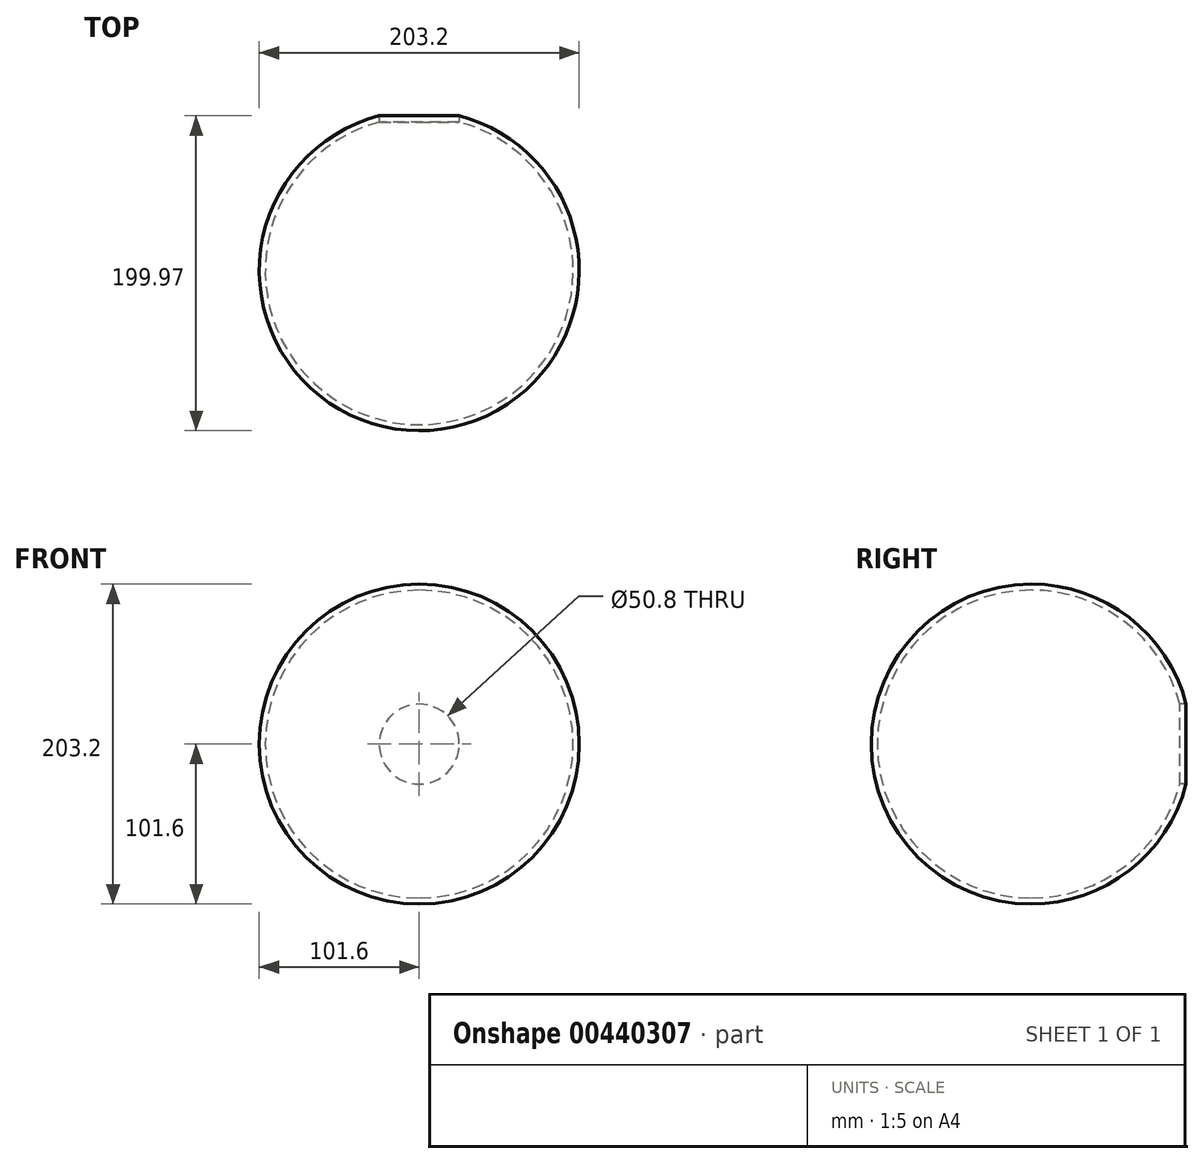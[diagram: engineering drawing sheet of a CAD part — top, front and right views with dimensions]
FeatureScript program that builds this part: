
annotation { "Feature Type Name" : "Feature", "Feature Type Description" : "" }
export const myFeature = defineFeature(function(context is Context, id is Id, definition is map)
    precondition{}
    {
        {
            var Q0;
            Q0=qCreatedBy(makeId("Front.planeOp"),FACE);
            var sketch = newSketch(context, id + "F0", { "sketchPlane" : qUnion([Q0])});
            skArc(sketch, "E0", {"start": v(0, -101.6) * mm, "mid": v(101.6, 0) * mm, "end": v(0, 101.6) * mm});
            skLineSegment(sketch, "E1", {"start": v(0, -97.8) * mm, "end": v(0, -101.6) * mm});
            skLineSegment(sketch, "E2", {"start": v(0, -101.6) * mm, "end": v(0, -97.8) * mm});
            skArc(sketch, "E3", {"start": v(0, -97.8) * mm, "mid": v(97.8, 0) * mm, "end": v(0, 97.8) * mm});
            skLineSegment(sketch, "E4.trimOffspring", {"start": v(0, 97.8) * mm, "end": v(0, 101.6) * mm});
            skSolve(sketch);
        }
        {
            var Q0;
            Q0=qCreatedBy(makeId("Front.planeOp"),FACE);
            var sketch = newSketch(context, id + "F1", { "sketchPlane" : qUnion([Q0])});
            skCircle(sketch, "E5", {"center": v(0, 0) * mm, "radius": 25.4 * mm});
            skLineSegment(sketch, "E6", {"start": v(0, 0) * mm, "end": v(0, 25.4) * mm});
            skSolve(sketch);
        }
        {
            var Q0;
            Q0 = qBodyType(qCreatedBy(id + "F1" ,EDGE), BodyType.WIRE);
            cPlane(context, id + "F2", {"entities" : qUnion([Q0]), "cplaneType" : CPlaneType.LINE_ANGLE, "offset" : 25 * mm, "angle" : 45 * degree, "width" : 150 * mm, "height" : 150 * mm});
        }
        {
            var Q0;
            {var subQ0=sQuery(id+"F0.wireOp",EDGE,"E0");Q0=makeQuery(id+"F0.imprint","IMPRINT",FACE,{"disambiguationData":[TD([[makeQuery(id+"F0.imprint","IMPRINT",EDGE,{"derivedFrom":subQ0}),1.0]])]});}
            var Q1;
            Q1=sQuery(id+"F0.wireOp",EDGE,"E2");
            revolve(context, id + "F3", {"entities" : qUnion([Q0]), "axis" : qUnion([Q1]), "revolveType" : RevolveType.FULL});
        }
        {
            var Q0;
            Q0 = qSketchRegion(id + "F1", true);
            extrude(context, id + "F4", {"entities" : qUnion([Q0]), "operationType" : NewBodyOperationType.REMOVE, "oppositeDirection" : true, "depth" : 318 * mm});
        }
    });
